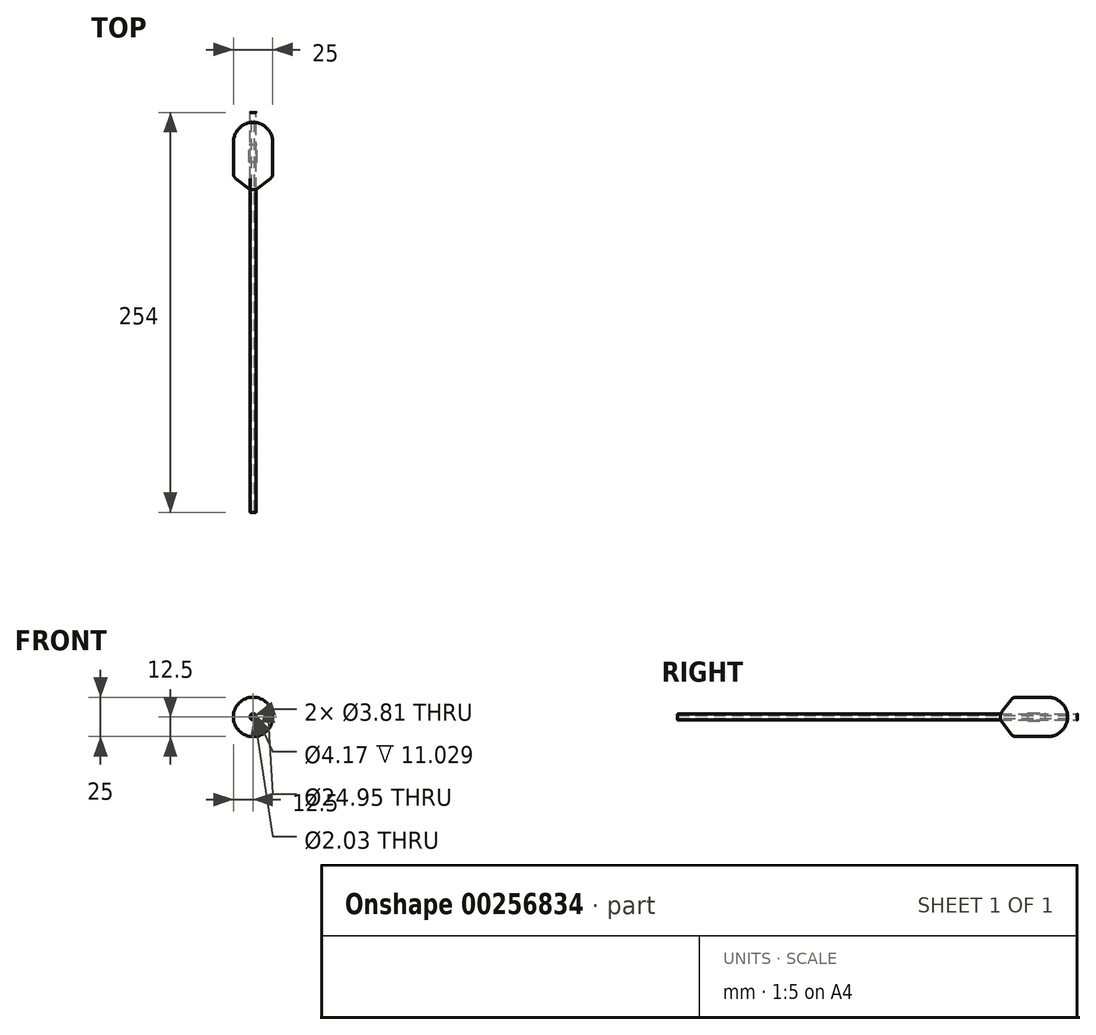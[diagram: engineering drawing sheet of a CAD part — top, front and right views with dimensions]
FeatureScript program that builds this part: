
annotation { "Feature Type Name" : "Feature", "Feature Type Description" : "" }
export const myFeature = defineFeature(function(context is Context, id is Id, definition is map)
    precondition{}
    {
        {
            var Q0;
            Q0=qCreatedBy(makeId("Front.planeOp"),FACE);
            var sketch = newSketch(context, id + "F0", { "sketchPlane" : qUnion([Q0])});
            skCircle(sketch, "E0", {"center": v(0, 0) * mm, "radius": 1.02 * mm});
            skCircle(sketch, "E1", {"center": v(0, 0) * mm, "radius": 1.9 * mm});
            skSolve(sketch);
        }
        {
            var Q0;
            Q0=makeQuery(id+"F0.imprint","IMPRINT",FACE,{"disambiguationData":[TD([[makeQuery(id+"F0.imprint","IMPRINT",EDGE,{"derivedFrom":sQuery(id+"F0.wireOp",EDGE,"E0")}),-1.0]])]});
            extrude(context, id + "F1", {"entities" : qUnion([Q0]), "depth" : 254 * mm});
        }
        {
            var Q0;
            Q0=makeQuery(id+"F1.opExtrude","CAP_EDGE",EDGE,{"disambiguationData":[OSD([sQuery(id+"F0.wireOp",EDGE,"E0")])],"isStart":true});
            chamfer(context, id + "F2", {"entities" : qUnion([Q0]), "width" : 0.56 * mm, "tangentPropagation" : true});
        }
        {
            var Q0;
            Q0=makeQuery(id+"F1.opExtrude","CAP_EDGE",EDGE,{"disambiguationData":[OSD([sQuery(id+"F0.wireOp",EDGE,"E1")])],"isStart":true});
            fillet(context, id + "F3", {"entities" : qUnion([Q0]), "radius" : 0.13 * mm, "tangentPropagation" : true, "allowEdgeOverflow" : false});
        }
        {
            var Q0;
            Q0=makeQuery(id+"F1.opExtrude","CAP_EDGE",EDGE,{"disambiguationData":[OSD([sQuery(id+"F0.wireOp",EDGE,"E1")])],"isStart":false});
            fillet(context, id + "F4", {"entities" : qUnion([Q0]), "radius" : 0.13 * mm, "tangentPropagation" : true, "allowEdgeOverflow" : false});
        }
        {
            var Q0;
            Q0=qCreatedBy(makeId("Right.planeOp"),FACE);
            var sketch = newSketch(context, id + "F5", { "sketchPlane" : qUnion([Q0])});
            skLineSegment(sketch, "E2", {"start": v(0, 0) * mm, "end": v(-318.3, 0) * mm, "construction": true});
            skSolve(sketch);
        }
        {
            var Q0;
            Q0=qCreatedBy(makeId("Right.planeOp"),FACE);
            var sketch = newSketch(context, id + "F6", { "sketchPlane" : qUnion([Q0])});
            skLineSegment(sketch, "E3.0", {"start": v(-253.87, 0) * mm, "end": v(-253.87, -1.9) * mm, "construction": true});
            skLineSegment(sketch, "E4", {"start": v(-49.05, 1.9) * mm, "end": v(-49.02, 1.9) * mm});
            skLineSegment(sketch, "E5", {"start": v(-49.05, 1.9) * mm, "end": v(-42.06, 11) * mm});
            skLineSegment(sketch, "E6", {"start": v(-39.04, 12.5) * mm, "end": v(-19.05, 12.5) * mm});
            skLineSegment(sketch, "E7.0", {"start": v(0, 0) * mm, "end": v(-318.3, 0) * mm, "construction": true});
            skLineSegment(sketch, "E8", {"start": v(-49.02, 1.9) * mm, "end": v(-42.05, 10.98) * mm});
            skLineSegment(sketch, "E9", {"start": v(-39.03, 12.47) * mm, "end": v(-19.05, 12.47) * mm});
            skPoint(sketch, "E10.orphan", {"position": v(-253.87, 1.9) * mm});
            skPoint(sketch, "E11.orphan", {"position": v(-40.92, 1.9) * mm});
            skPoint(sketch, "E12.visualSharp", {"position": v(-40.92, 12.5) * mm});
            skArc(sketch, "E12.filletArc", {"start": v(-39.04, 12.5) * mm, "mid": v(-40.73, 12.1) * mm, "end": v(-42.06, 11) * mm});
            skPoint(sketch, "E13.visualSharp", {"position": v(-40.9, 12.47) * mm});
            skArc(sketch, "E13.filletArc", {"start": v(-39.03, 12.47) * mm, "mid": v(-40.71, 12.08) * mm, "end": v(-42.05, 10.98) * mm});
            skLineSegment(sketch, "E14", {"start": v(-29.04, 12.5) * mm, "end": v(-29.04, -17.87) * mm, "construction": true});
            skArc(sketch, "E15", {"start": v(-19.05, 12.47) * mm, "mid": v(-10.8, 9.49) * mm, "end": v(-6.38, 1.9) * mm});
            skArc(sketch, "E16", {"start": v(-19.05, 12.5) * mm, "mid": v(-10.78, 9.5) * mm, "end": v(-6.35, 1.9) * mm});
            skLineSegment(sketch, "E17", {"start": v(-6.38, 1.9) * mm, "end": v(-6.35, 1.9) * mm});
            skSolve(sketch);
        }
        {
            var Q0;
            Q0=qSketchRegion(id+"F6",true);
            var Q1;
            Q1=sQuery(id+"F6.wireOp",EDGE,"E7.0");
            revolve(context, id + "F7", {"entities" : qUnion([Q0]), "axis" : qUnion([Q1]), "revolveType" : RevolveType.FULL});
        }
        {
            var Q0;
            Q0=qCreatedBy(makeId("Front.planeOp"),FACE);
            cPlane(context, id + "F8", {"entities" : qUnion([Q0]), "cplaneType" : CPlaneType.OFFSET, "offset" : 20.42 * mm, "width" : 152.4 * mm, "height" : 152.4 * mm});
        }
        {
            var Q0;
            Q0=qCreatedBy(makeId("Front.planeOp"),FACE);
            cPlane(context, id + "F9", {"entities" : qUnion([Q0]), "cplaneType" : CPlaneType.OFFSET, "offset" : 31.45 * mm, "width" : 152.4 * mm, "height" : 152.4 * mm});
        }
        {
            var Q0;
            Q0=qCreatedBy(id+"F9.planeOp",FACE);
            var sketch = newSketch(context, id + "F10", { "sketchPlane" : qUnion([Q0])});
            skCircle(sketch, "E18.0", {"center": v(0, 0) * mm, "radius": 12.5 * mm, "construction": true});
            skArc(sketch, "E19", {"start": v(-10.13, 7.33) * mm, "mid": v(0, 12.5) * mm, "end": v(10.13, 7.33) * mm});
            skLineSegment(sketch, "E20", {"start": v(0, 18.59) * mm, "end": v(0, -14.82) * mm, "construction": true});
            skLineSegment(sketch, "E21", {"start": v(-18.7, 0) * mm, "end": v(23.1, 0) * mm, "construction": true});
            skArc(sketch, "E22.MirrorCS", {"start": v(-10.13, -7.33) * mm, "mid": v(0, -12.5) * mm, "end": v(10.13, -7.33) * mm});
            skArc(sketch, "E23", {"start": v(-10.55, 6.7) * mm, "mid": v(-12.5, 0) * mm, "end": v(-10.55, -6.7) * mm});
            skArc(sketch, "E24.MirrorCS", {"start": v(10.55, 6.7) * mm, "mid": v(12.5, 0) * mm, "end": v(10.55, -6.7) * mm});
            skSolve(sketch);
        }
        {
            var Q0;
            Q0=qCreatedBy(id+"F8.planeOp",FACE);
            var sketch = newSketch(context, id + "F11", { "sketchPlane" : qUnion([Q0])});
            skCircle(sketch, "E25.0", {"center": v(0, 0) * mm, "radius": 12.5 * mm, "construction": true});
            skArc(sketch, "E26", {"start": v(-10.13, 7.33) * mm, "mid": v(0, 12.5) * mm, "end": v(10.13, 7.33) * mm});
            skLineSegment(sketch, "E27", {"start": v(0, 18.32) * mm, "end": v(0, -15.1) * mm, "construction": true});
            skLineSegment(sketch, "E28", {"start": v(-19.02, 0) * mm, "end": v(22.78, 0) * mm, "construction": true});
            skArc(sketch, "E29.MirrorCS", {"start": v(-10.13, -7.33) * mm, "mid": v(0, -12.5) * mm, "end": v(10.13, -7.33) * mm});
            skArc(sketch, "E30", {"start": v(-10.55, 6.7) * mm, "mid": v(-12.5, 0) * mm, "end": v(-10.55, -6.7) * mm});
            skArc(sketch, "E31.MirrorCS", {"start": v(10.55, 6.7) * mm, "mid": v(12.5, 0) * mm, "end": v(10.55, -6.7) * mm});
            skSolve(sketch);
        }
        {
            var Q0;
            Q0=qCreatedBy(id+"F8.planeOp",FACE);
            var sketch = newSketch(context, id + "F12", { "sketchPlane" : qUnion([Q0])});
            skCircle(sketch, "E32", {"center": v(0, 0) * mm, "radius": 2.47 * mm});
            skCircle(sketch, "E33", {"center": v(0, 0) * mm, "radius": 2.08 * mm});
            skSolve(sketch);
        }
        {
            var Q0;
            Q0=qSketchRegion(id+"F12",true);
            var Q1;
            Q1=qCreatedBy(id+"F9.planeOp",FACE);
            extrude(context, id + "F13", {"entities" : qUnion([Q0]), "operationType" : NewBodyOperationType.ADD, "endBound" : BoundingType.UP_TO_SURFACE, "endBoundEntityFace" : qUnion([Q1]), "depth" : 25.4 * mm});
        }
    });
